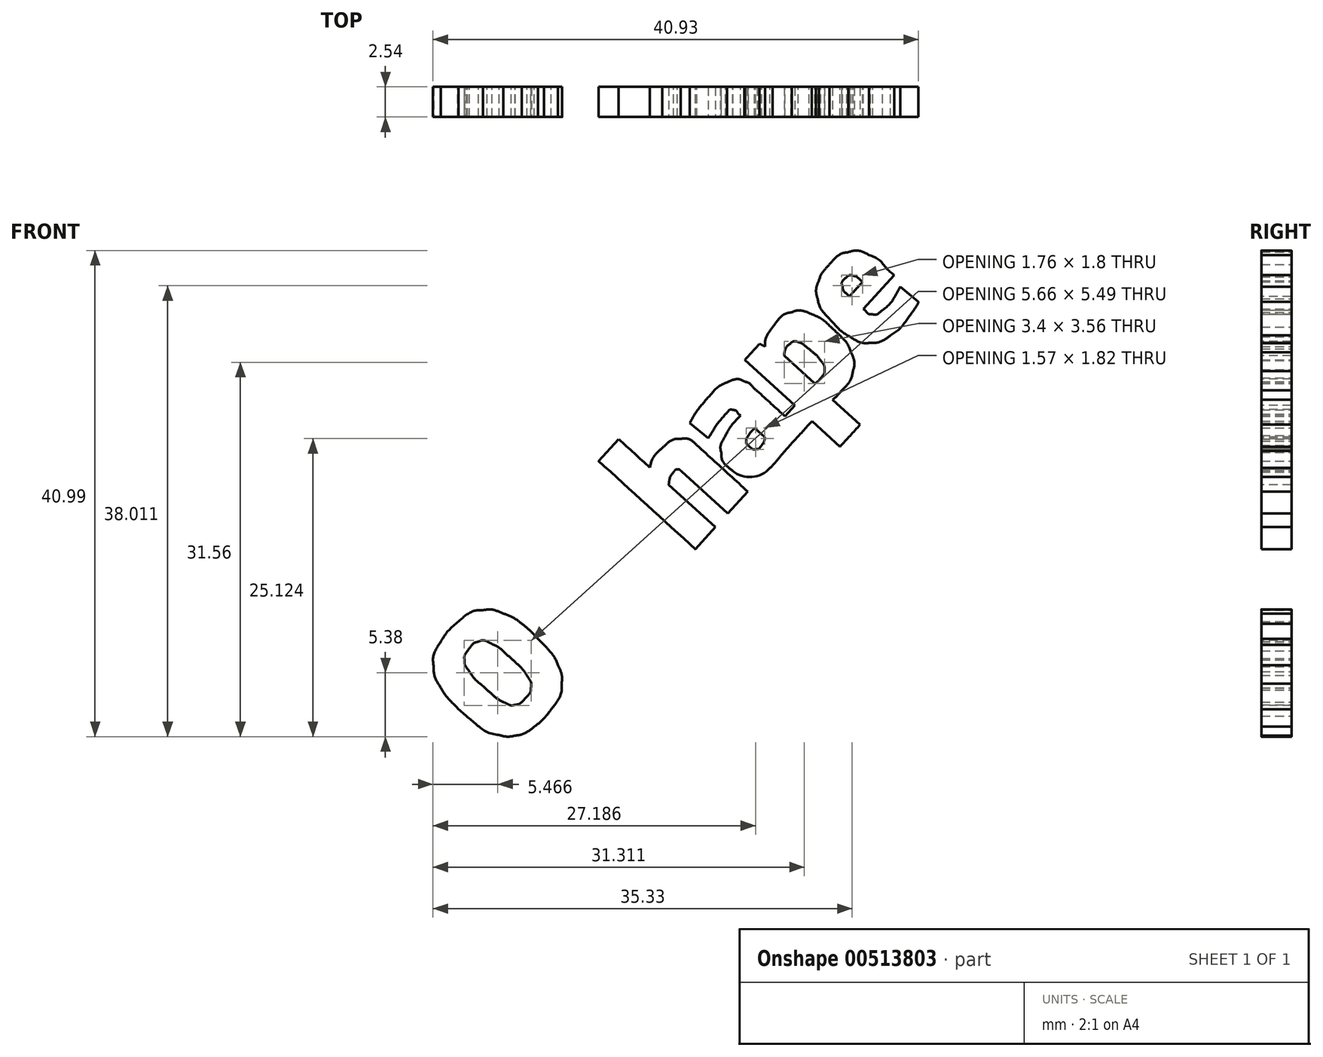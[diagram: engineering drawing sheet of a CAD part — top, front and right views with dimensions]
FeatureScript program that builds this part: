
annotation { "Feature Type Name" : "Feature", "Feature Type Description" : "" }
export const myFeature = defineFeature(function(context is Context, id is Id, definition is map)
    precondition{}
    {
        {
            var Q0;
            Q0=qCreatedBy(makeId("Front.planeOp"),FACE);
            var sketch = newSketch(context, id + "F0", { "sketchPlane" : qUnion([Q0])});
            skLineSegment(sketch, "E0", {"start": v(-53.27, 10.23) * mm, "end": v(-36.43, 28.71) * mm});
            skFitSpline(sketch, "E1", {"points": [v(-36.43, 28.71) * mm, v(-27.64, 20.71) * mm, v(-18.87, 12.7) * mm, v(-10.08, 4.7) * mm]});
            skFitSpline(sketch, "E2", {"points": [v(-10.08, 4.7) * mm, v(-8.44, 11.15) * mm, v(-4.52, 16.83) * mm, v(0.34, 21.3) * mm]});
            skFitSpline(sketch, "E3", {"points": [v(0.34, 21.3) * mm, v(4.57, 25.2) * mm, v(9.8, 28.49) * mm, v(15.67, 28.9) * mm]});
            skFitSpline(sketch, "E4", {"points": [v(15.67, 28.9) * mm, v(20.8, 29.27) * mm, v(25.8, 26.98) * mm, v(29.52, 23.56) * mm]});
            skFitSpline(sketch, "E5", {"points": [v(29.52, 23.56) * mm, v(43.78, 10.53) * mm, v(58.1, -2.45) * mm, v(72.33, -15.5) * mm]});
            skFitSpline(sketch, "E6", {"points": [v(72.33, -15.5) * mm, v(66.71, -21.65) * mm, v(61.11, -27.81) * mm, v(55.5, -33.96) * mm]});
            skFitSpline(sketch, "E7", {"points": [v(55.5, -33.96) * mm, v(42.52, -22.13) * mm, v(29.54, -10.3) * mm, v(16.56, 1.53) * mm]});
            skFitSpline(sketch, "E8", {"points": [v(16.56, 1.53) * mm, v(15.6, 2.38) * mm, v(14.46, 3.32) * mm, v(13.1, 3.21) * mm]});
            skFitSpline(sketch, "E9", {"points": [v(13.1, 3.21) * mm, v(11.64, 3.07) * mm, v(10.56, 1.91) * mm, v(9.69, 0.84) * mm]});
            skFitSpline(sketch, "E10", {"points": [v(9.69, 0.84) * mm, v(7.37, -2.2) * mm, v(6.21, -5.96) * mm, v(5.73, -9.7) * mm]});
            skFitSpline(sketch, "E11", {"points": [v(5.73, -9.7) * mm, v(18.8, -21.64) * mm, v(31.9, -33.56) * mm, v(44.98, -45.5) * mm]});
            skFitSpline(sketch, "E12", {"points": [v(44.98, -45.5) * mm, v(39.37, -51.66) * mm, v(33.75, -57.82) * mm, v(28.14, -63.97) * mm]});
            skFitSpline(sketch, "E13", {"points": [v(28.14, -63.97) * mm, v(1, -39.24) * mm, v(-26.13, -14.5) * mm, v(-53.27, 10.23) * mm]});
            skFitSpline(sketch, "E14", {"points": [v(-186.33, -141.9) * mm, v(-182.32, -135.58) * mm, v(-177.27, -129.94) * mm, v(-171.6, -125.06) * mm]});
            skFitSpline(sketch, "E15", {"points": [v(-171.6, -125.06) * mm, v(-165.71, -120.05) * mm, v(-158.56, -116.1) * mm, v(-150.74, -115.42) * mm]});
            skFitSpline(sketch, "E16", {"points": [v(-150.74, -115.42) * mm, v(-144.9, -114.85) * mm, v(-139.02, -116.11) * mm, v(-133.65, -118.36) * mm]});
            skFitSpline(sketch, "E17", {"points": [v(-133.65, -118.36) * mm, v(-126.81, -120.95) * mm, v(-120.6, -124.93) * mm, v(-114.78, -129.3) * mm]});
            skFitSpline(sketch, "E18", {"points": [v(-120.21, -125.1) * mm, v(-114.66, -129.62) * mm, v(-109.39, -134.5) * mm, v(-104.55, -139.78) * mm]});
            skFitSpline(sketch, "E19", {"points": [v(-99.47, -144.6) * mm, v(-94.8, -149.75) * mm, v(-90.53, -155.38) * mm, v(-87.66, -161.75) * mm]});
            skFitSpline(sketch, "E20", {"points": [v(-87.66, -161.75) * mm, v(-85.46, -166.63) * mm, v(-84.22, -172) * mm, v(-84.54, -177.37) * mm]});
            skFitSpline(sketch, "E21", {"points": [v(-84.54, -177.37) * mm, v(-84.95, -185.4) * mm, v(-88.7, -192.85) * mm, v(-93.46, -199.17) * mm]});
            skFitSpline(sketch, "E22", {"points": [v(-93.46, -199.17) * mm, v(-97.55, -204.52) * mm, v(-102.2, -209.48) * mm, v(-107.55, -213.6) * mm]});
            skFitSpline(sketch, "E23", {"points": [v(-107.55, -213.6) * mm, v(-112.33, -217.28) * mm, v(-117.85, -220.17) * mm, v(-123.83, -221.24) * mm]});
            skFitSpline(sketch, "E24", {"points": [v(-123.83, -221.24) * mm, v(-128.3, -222.06) * mm, v(-132.96, -221.8) * mm, v(-137.37, -220.7) * mm]});
            skFitSpline(sketch, "E25", {"points": [v(-137.37, -220.7) * mm, v(-147.8, -218.04) * mm, v(-156.69, -211.53) * mm, v(-164.86, -204.77) * mm]});
            skLineSegment(sketch, "E26", {"start": v(-164.86, -204.77) * mm, "end": v(-172.01, -198.25) * mm});
            skFitSpline(sketch, "E27", {"points": [v(-172.01, -198.25) * mm, v(-177.2, -193.04) * mm, v(-182.25, -187.58) * mm, v(-186.12, -181.29) * mm]});
            skFitSpline(sketch, "E28", {"points": [v(-186.12, -181.29) * mm, v(-189.52, -175.81) * mm, v(-192.02, -169.62) * mm, v(-192.4, -163.13) * mm]});
            skFitSpline(sketch, "E29", {"points": [v(-192.4, -163.13) * mm, v(-192.9, -155.61) * mm, v(-190.31, -148.2) * mm, v(-186.33, -141.9) * mm]});
            skFitSpline(sketch, "E30", {"points": [v(-164.02, -149.89) * mm, v(-165.55, -152.09) * mm, v(-166.58, -154.74) * mm, v(-166.4, -157.46) * mm]});
            skFitSpline(sketch, "E31", {"points": [v(-166.4, -157.46) * mm, v(-166.2, -161.13) * mm, v(-164.3, -164.44) * mm, v(-162.22, -167.37) * mm]});
            skFitSpline(sketch, "E32", {"points": [v(-162.22, -167.37) * mm, v(-157.95, -173.21) * mm, v(-152.58, -178.12) * mm, v(-147.22, -182.95) * mm]});
            skFitSpline(sketch, "E33", {"points": [v(-147.22, -182.95) * mm, v(-142.97, -186.63) * mm, v(-138.6, -190.25) * mm, v(-133.62, -192.9) * mm]});
            skFitSpline(sketch, "E34", {"points": [v(-133.62, -192.9) * mm, v(-130.57, -194.5) * mm, v(-127.07, -195.74) * mm, v(-123.58, -195.13) * mm]});
            skFitSpline(sketch, "E35", {"points": [v(-123.58, -195.13) * mm, v(-120.22, -194.56) * mm, v(-117.48, -192.3) * mm, v(-115.22, -189.88) * mm]});
            skFitSpline(sketch, "E36", {"points": [v(-115.22, -189.88) * mm, v(-112.92, -187.36) * mm, v(-110.77, -184.36) * mm, v(-110.47, -180.85) * mm]});
            skFitSpline(sketch, "E37", {"points": [v(-110.47, -180.85) * mm, v(-110.14, -177.1) * mm, v(-111.87, -173.56) * mm, v(-113.88, -170.52) * mm]});
            skFitSpline(sketch, "E38", {"points": [v(-113.88, -170.52) * mm, v(-117.56, -165.1) * mm, v(-122.34, -160.58) * mm, v(-127.1, -156.13) * mm]});
            skFitSpline(sketch, "E39", {"points": [v(-127.1, -156.13) * mm, v(-132.17, -151.63) * mm, v(-137.33, -147.07) * mm, v(-143.37, -143.9) * mm]});
            skFitSpline(sketch, "E40", {"points": [v(-143.37, -143.9) * mm, v(-146.8, -142.1) * mm, v(-150.9, -140.83) * mm, v(-154.74, -142.07) * mm]});
            skFitSpline(sketch, "E41", {"points": [v(-154.74, -142.07) * mm, v(-158.68, -143.4) * mm, v(-161.63, -146.62) * mm, v(-164.02, -149.89) * mm]});
            skFitSpline(sketch, "E42", {"points": [v(-104.03, -102.52) * mm, v(-103.02, -94.53) * mm, v(-99.15, -87) * mm, v(-93.41, -81.38) * mm]});
            skFitSpline(sketch, "E43", {"points": [v(-93.41, -81.38) * mm, v(-89.05, -77.02) * mm, v(-83.58, -73.2) * mm, v(-77.29, -72.58) * mm]});
            skFitSpline(sketch, "E44", {"points": [v(-77.29, -72.58) * mm, v(-72.12, -72.02) * mm, v(-67.02, -74.23) * mm, v(-63.2, -77.62) * mm]});
            skFitSpline(sketch, "E45", {"points": [v(-63.2, -77.62) * mm, v(-53.68, -86.29) * mm, v(-44.17, -94.97) * mm, v(-34.64, -103.65) * mm]});
            skFitSpline(sketch, "E46", {"points": [v(-10.06, -76.67) * mm, v(-9.19, -75.62) * mm, v(-8.13, -74.65) * mm, v(-7.6, -73.37) * mm]});
            skFitSpline(sketch, "E47", {"points": [v(-7.6, -73.37) * mm, v(-7.12, -72.25) * mm, v(-8.15, -71.15) * mm, v(-9.12, -70.75) * mm]});
            skFitSpline(sketch, "E48", {"points": [v(-9.12, -70.75) * mm, v(-10.63, -70.2) * mm, v(-12.23, -70.8) * mm, v(-13.63, -71.35) * mm]});
            skFitSpline(sketch, "E49", {"points": [v(-13.63, -71.35) * mm, v(-17.16, -72.88) * mm, v(-20.68, -74.43) * mm, v(-24.2, -75.97) * mm]});
            skFitSpline(sketch, "E50", {"points": [v(-24.2, -75.97) * mm, v(-27.72, -77.47) * mm, v(-31.17, -79.28) * mm, v(-35, -79.83) * mm]});
            skFitSpline(sketch, "E51", {"points": [v(-35, -79.83) * mm, v(-40.54, -80.8) * mm, v(-46.38, -79.42) * mm, v(-51.02, -76.27) * mm]});
            skFitSpline(sketch, "E52", {"points": [v(-51.02, -76.27) * mm, v(-55.75, -73.06) * mm, v(-59.9, -68.53) * mm, v(-61.46, -62.93) * mm]});
            skFitSpline(sketch, "E53", {"points": [v(-61.46, -62.93) * mm, v(-62.78, -58.27) * mm, v(-62.02, -53.26) * mm, v(-60.19, -48.85) * mm]});
            skFitSpline(sketch, "E54", {"points": [v(-60.19, -48.85) * mm, v(-57.48, -42.27) * mm, v(-52.9, -36.68) * mm, v(-48.03, -31.57) * mm]});
            skFitSpline(sketch, "E55", {"points": [v(-48.03, -31.57) * mm, v(-43.95, -27.33) * mm, v(-39.76, -23.17) * mm, v(-35.17, -19.47) * mm]});
            skFitSpline(sketch, "E56", {"points": [v(-35.17, -19.47) * mm, v(-30.45, -24.14) * mm, v(-25.78, -28.86) * mm, v(-21.09, -33.56) * mm]});
            skFitSpline(sketch, "E57", {"points": [v(-21.09, -33.56) * mm, v(-24.53, -36.31) * mm, v(-27.72, -39.36) * mm, v(-30.85, -42.46) * mm]});
            skFitSpline(sketch, "E58", {"points": [v(-30.85, -42.46) * mm, v(-32.92, -44.54) * mm, v(-35, -46.61) * mm, v(-36.84, -48.9) * mm]});
            skFitSpline(sketch, "E59", {"points": [v(-36.84, -48.9) * mm, v(-37.61, -49.94) * mm, v(-38.46, -51.03) * mm, v(-38.61, -52.35) * mm]});
            skFitSpline(sketch, "E60", {"points": [v(-38.61, -52.35) * mm, v(-38.74, -53.52) * mm, v(-37.78, -54.45) * mm, v(-36.82, -54.95) * mm]});
            skFitSpline(sketch, "E61", {"points": [v(-36.82, -54.95) * mm, v(-35.8, -55.43) * mm, v(-34.65, -55.1) * mm, v(-33.66, -54.72) * mm]});
            skFitSpline(sketch, "E62", {"points": [v(-33.66, -54.72) * mm, v(-27.51, -52.21) * mm, v(-21.4, -49.63) * mm, v(-15.25, -47.13) * mm]});
            skFitSpline(sketch, "E63", {"points": [v(-15.25, -47.13) * mm, v(-10.1, -45.1) * mm, v(-4.15, -44.97) * mm, v(0.92, -47.28) * mm]});
            skFitSpline(sketch, "E64", {"points": [v(0.92, -47.28) * mm, v(5.88, -49.54) * mm, v(10.08, -53.4) * mm, v(12.97, -58) * mm]});
            skFitSpline(sketch, "E65", {"points": [v(12.97, -58) * mm, v(16.03, -62.29) * mm, v(17.14, -67.82) * mm, v(16.14, -72.98) * mm]});
            skFitSpline(sketch, "E66", {"points": [v(-36.98, -135.4) * mm, v(-50.22, -123.37) * mm, v(-63.42, -111.28) * mm, v(-76.67, -99.25) * mm]});
            skFitSpline(sketch, "E67", {"points": [v(-76.67, -99.25) * mm, v(-77.91, -98.04) * mm, v(-79.99, -97.82) * mm, v(-81.29, -99.06) * mm]});
            skFitSpline(sketch, "E68", {"points": [v(-81.29, -99.06) * mm, v(-84.7, -102.09) * mm, v(-86.12, -106.73) * mm, v(-86.73, -111.12) * mm]});
            skFitSpline(sketch, "E69", {"points": [v(-86.73, -111.12) * mm, v(-73.65, -123.06) * mm, v(-60.55, -134.98) * mm, v(-47.47, -146.91) * mm]});
            skFitSpline(sketch, "E70", {"points": [v(-47.47, -146.91) * mm, v(-53.1, -153.09) * mm, v(-58.72, -159.25) * mm, v(-64.34, -165.42) * mm]});
            skFitSpline(sketch, "E71", {"points": [v(-120.95, -113.82) * mm, v(-116.84, -109.3) * mm, v(-112.71, -104.79) * mm, v(-108.6, -100.27) * mm]});
            skFitSpline(sketch, "E72", {"points": [v(-108.6, -100.27) * mm, v(-107.07, -101.02) * mm, v(-105.55, -101.77) * mm, v(-104.03, -102.52) * mm]});
            skFitSpline(sketch, "E73", {"points": [v(23.54, 42.35) * mm, v(27.53, 49.45) * mm, v(32.32, 56.09) * mm, v(37.57, 62.3) * mm]});
            skFitSpline(sketch, "E74", {"points": [v(37.57, 62.3) * mm, v(42.46, 67.97) * mm, v(48.03, 73.34) * mm, v(54.92, 76.47) * mm]});
            skFitSpline(sketch, "E75", {"points": [v(54.92, 76.47) * mm, v(59.47, 78.56) * mm, v(64.89, 79.24) * mm, v(69.62, 77.33) * mm]});
            skFitSpline(sketch, "E76", {"points": [v(69.62, 77.33) * mm, v(73.88, 75.73) * mm, v(76.98, 72.26) * mm, v(80.3, 69.33) * mm]});
            skFitSpline(sketch, "E77", {"points": [v(80.3, 69.33) * mm, v(88.09, 62.24) * mm, v(95.86, 55.14) * mm, v(103.65, 48.05) * mm]});
            skFitSpline(sketch, "E78", {"points": [v(103.65, 48.05) * mm, v(106.44, 51.12) * mm, v(109.23, 54.18) * mm, v(112.02, 57.24) * mm]});
            skFitSpline(sketch, "E79", {"points": [v(112.02, 57.24) * mm, v(98, 70.03) * mm, v(83.97, 82.8) * mm, v(69.95, 95.6) * mm]});
            skFitSpline(sketch, "E80", {"points": [v(69.95, 95.6) * mm, v(74.07, 100.1) * mm, v(78.18, 104.63) * mm, v(82.3, 109.13) * mm]});
            skFitSpline(sketch, "E81", {"points": [v(82.3, 109.13) * mm, v(83.82, 108.38) * mm, v(85.35, 107.63) * mm, v(86.88, 106.89) * mm]});
            skFitSpline(sketch, "E82", {"points": [v(86.88, 106.89) * mm, v(87.24, 112.8) * mm, v(89.9, 118.34) * mm, v(93.32, 123.1) * mm]});
            skFitSpline(sketch, "E83", {"points": [v(93.32, 123.1) * mm, v(97.36, 128.62) * mm, v(102.62, 133.75) * mm, v(109.37, 135.66) * mm]});
            skFitSpline(sketch, "E84", {"points": [v(109.37, 135.66) * mm, v(114.94, 137.28) * mm, v(120.96, 136.3) * mm, v(126.2, 134) * mm]});
            skFitSpline(sketch, "E85", {"points": [v(126.2, 134) * mm, v(133.7, 130.74) * mm, v(140.1, 125.47) * mm, v(146.02, 119.92) * mm]});
            skFitSpline(sketch, "E86", {"points": [v(146.02, 119.92) * mm, v(151.44, 114.7) * mm, v(156.47, 108.83) * mm, v(159.4, 101.83) * mm]});
            skFitSpline(sketch, "E87", {"points": [v(159.4, 101.83) * mm, v(161.5, 96.85) * mm, v(162.2, 91.23) * mm, v(160.95, 85.94) * mm]});
            skFitSpline(sketch, "E88", {"points": [v(160.95, 85.94) * mm, v(159.56, 79.83) * mm, v(156.01, 74.43) * mm, v(151.82, 69.86) * mm]});
            skFitSpline(sketch, "E89", {"points": [v(151.82, 69.86) * mm, v(149.32, 67.12) * mm, v(146.73, 64.47) * mm, v(143.9, 62.07) * mm]});
            skFitSpline(sketch, "E90", {"points": [v(143.9, 62.07) * mm, v(151.63, 55.03) * mm, v(159.36, 47.98) * mm, v(167.09, 40.94) * mm]});
            skFitSpline(sketch, "E91", {"points": [v(167.09, 40.94) * mm, v(161.47, 34.76) * mm, v(155.84, 28.6) * mm, v(150.22, 22.43) * mm]});
            skFitSpline(sketch, "E92", {"points": [v(150.22, 22.43) * mm, v(142.33, 29.61) * mm, v(134.45, 36.8) * mm, v(126.56, 43.99) * mm]});
            skFitSpline(sketch, "E93", {"points": [v(126.56, 43.99) * mm, v(118.91, 35.6) * mm, v(111.25, 27.22) * mm, v(103.62, 18.81) * mm]});
            skFitSpline(sketch, "E94", {"points": [v(103.62, 18.81) * mm, v(99.56, 13.9) * mm, v(95.51, 8.97) * mm, v(91.11, 4.37) * mm]});
            skFitSpline(sketch, "E95", {"points": [v(59.52, 2.02) * mm, v(54.7, 5.92) * mm, v(50.7, 11.35) * mm, v(49.95, 17.64) * mm]});
            skFitSpline(sketch, "E96", {"points": [v(49.95, 17.64) * mm, v(49.3, 22.63) * mm, v(51.31, 27.47) * mm, v(53.6, 31.79) * mm]});
            skFitSpline(sketch, "E97", {"points": [v(53.6, 31.79) * mm, v(57, 37.98) * mm, v(61.42, 43.54) * mm, v(66.15, 48.75) * mm]});
            skFitSpline(sketch, "E98", {"points": [v(66.15, 48.75) * mm, v(64.17, 50.33) * mm, v(62.57, 52.7) * mm, v(59.97, 53.27) * mm]});
            skFitSpline(sketch, "E99", {"points": [v(59.97, 53.27) * mm, v(57.4, 53.67) * mm, v(55.35, 51.63) * mm, v(53.74, 49.92) * mm]});
            skFitSpline(sketch, "E100", {"points": [v(53.74, 49.92) * mm, v(48.26, 43.55) * mm, v(43.43, 36.64) * mm, v(39.1, 29.44) * mm]});
            skFitSpline(sketch, "E101", {"points": [v(39.1, 29.44) * mm, v(33.91, 33.75) * mm, v(28.72, 38.05) * mm, v(23.54, 42.35) * mm]});
            skFitSpline(sketch, "E102", {"points": [v(103.13, 99.24) * mm, v(111.74, 91.4) * mm, v(120.34, 83.54) * mm, v(128.96, 75.7) * mm]});
            skFitSpline(sketch, "E103", {"points": [v(128.96, 75.7) * mm, v(130.89, 76.93) * mm, v(132.55, 78.55) * mm, v(134, 80.32) * mm]});
            skFitSpline(sketch, "E104", {"points": [v(134, 80.32) * mm, v(135.6, 82.3) * mm, v(136.93, 84.71) * mm, v(136.95, 87.33) * mm]});
            skFitSpline(sketch, "E105", {"points": [v(136.95, 87.33) * mm, v(136.97, 90.21) * mm, v(135.48, 92.84) * mm, v(133.8, 95.07) * mm]});
            skFitSpline(sketch, "E106", {"points": [v(133.8, 95.07) * mm, v(130.98, 98.7) * mm, v(127.5, 101.75) * mm, v(124.02, 104.72) * mm]});
            skFitSpline(sketch, "E107", {"points": [v(124.02, 104.72) * mm, v(121.2, 107) * mm, v(118.28, 109.32) * mm, v(114.81, 110.5) * mm]});
            skFitSpline(sketch, "E108", {"points": [v(114.81, 110.5) * mm, v(112.79, 111.22) * mm, v(110.4, 111.04) * mm, v(108.69, 109.68) * mm]});
            skFitSpline(sketch, "E109", {"points": [v(108.69, 109.68) * mm, v(105.5, 107.16) * mm, v(103.56, 103.24) * mm, v(103.13, 99.24) * mm]});
            skFitSpline(sketch, "E110", {"points": [v(72.95, 31.92) * mm, v(72, 30.49) * mm, v(71.1, 28.89) * mm, v(71.08, 27.12) * mm]});
            skFitSpline(sketch, "E111", {"points": [v(71.08, 27.12) * mm, v(71.12, 25.34) * mm, v(72.27, 23.79) * mm, v(73.54, 22.63) * mm]});
            skFitSpline(sketch, "E112", {"points": [v(73.54, 22.63) * mm, v(75.03, 21.3) * mm, v(76.92, 20.12) * mm, v(79, 20.26) * mm]});
            skFitSpline(sketch, "E113", {"points": [v(79, 20.26) * mm, v(81.13, 20.42) * mm, v(82.9, 21.93) * mm, v(84.13, 23.58) * mm]});
            skFitSpline(sketch, "E114", {"points": [v(84.13, 23.58) * mm, v(85.55, 25.6) * mm, v(86.56, 27.96) * mm, v(86.7, 30.44) * mm]});
            skFitSpline(sketch, "E115", {"points": [v(86.7, 30.44) * mm, v(83.85, 33.03) * mm, v(81, 35.63) * mm, v(78.16, 38.22) * mm]});
            skFitSpline(sketch, "E116", {"points": [v(78.16, 38.22) * mm, v(76.34, 36.2) * mm, v(74.49, 34.18) * mm, v(72.95, 31.92) * mm]});
            skFitSpline(sketch, "E117", {"points": [v(132.26, 162.28) * mm, v(134.22, 167.42) * mm, v(137.48, 171.96) * mm, v(141.15, 176) * mm]});
            skFitSpline(sketch, "E118", {"points": [v(141.15, 176) * mm, v(145.43, 180.8) * mm, v(150.85, 184.9) * mm, v(157.2, 186.37) * mm]});
            skFitSpline(sketch, "E119", {"points": [v(157.2, 186.37) * mm, v(163.06, 187.77) * mm, v(169.27, 186.6) * mm, v(174.6, 183.97) * mm]});
            skFitSpline(sketch, "E120", {"points": [v(174.6, 183.97) * mm, v(182.89, 180.01) * mm, v(189.07, 173.04) * mm, v(195.87, 167.1) * mm]});
            skFitSpline(sketch, "E121", {"points": [v(195.87, 167.1) * mm, v(187.17, 157.54) * mm, v(178.46, 148) * mm, v(169.76, 138.44) * mm]});
            skFitSpline(sketch, "E122", {"points": [v(169.76, 138.44) * mm, v(172.04, 136.48) * mm, v(174.48, 134.22) * mm, v(177.63, 133.94) * mm]});
            skFitSpline(sketch, "E123", {"points": [v(177.63, 133.94) * mm, v(180.8, 133.72) * mm, v(183.59, 135.62) * mm, v(185.91, 137.55) * mm]});
            skFitSpline(sketch, "E124", {"points": [v(185.91, 137.55) * mm, v(192.24, 142.96) * mm, v(196.9, 150.02) * mm, v(200.82, 157.3) * mm]});
            skFitSpline(sketch, "E125", {"points": [v(200.82, 157.3) * mm, v(205.97, 153.02) * mm, v(211.13, 148.76) * mm, v(216.27, 144.48) * mm]});
            skFitSpline(sketch, "E126", {"points": [v(216.27, 144.48) * mm, v(214.74, 141.13) * mm, v(212.67, 138.06) * mm, v(210.55, 135.06) * mm]});
            skFitSpline(sketch, "E127", {"points": [v(210.55, 135.06) * mm, v(205.48, 128) * mm, v(199.78, 121.22) * mm, v(192.65, 116.17) * mm]});
            skFitSpline(sketch, "E128", {"points": [v(192.65, 116.17) * mm, v(187.77, 112.72) * mm, v(182.03, 110.2) * mm, v(176, 109.99) * mm]});
            skFitSpline(sketch, "E129", {"points": [v(176, 109.99) * mm, v(169.84, 109.7) * mm, v(163.83, 111.86) * mm, v(158.63, 115) * mm]});
            skFitSpline(sketch, "E130", {"points": [v(158.63, 115) * mm, v(152.39, 118.8) * mm, v(146.98, 123.81) * mm, v(142.02, 129.13) * mm]});
            skFitSpline(sketch, "E131", {"points": [v(142.02, 129.13) * mm, v(137.33, 134.29) * mm, v(133.08, 140.17) * mm, v(131.31, 147.02) * mm]});
            skFitSpline(sketch, "E132", {"points": [v(131.31, 147.02) * mm, v(130, 152.04) * mm, v(130.38, 157.45) * mm, v(132.26, 162.28) * mm]});
            skFitSpline(sketch, "E133", {"points": [v(152.2, 157.45) * mm, v(152.95, 154.01) * mm, v(155.61, 151.46) * mm, v(157.96, 149) * mm]});
            skFitSpline(sketch, "E134", {"points": [v(157.96, 149) * mm, v(161.67, 153.07) * mm, v(165.37, 157.14) * mm, v(169.08, 161.2) * mm]});
            skFitSpline(sketch, "E135", {"points": [v(169.08, 161.2) * mm, v(166.82, 163.3) * mm, v(164.42, 165.5) * mm, v(161.4, 166.4) * mm]});
            skFitSpline(sketch, "E136", {"points": [v(161.4, 166.4) * mm, v(159.47, 167) * mm, v(157.29, 166.61) * mm, v(155.73, 165.33) * mm]});
            skFitSpline(sketch, "E137", {"points": [v(155.73, 165.33) * mm, v(153.47, 163.44) * mm, v(151.56, 160.51) * mm, v(152.2, 157.45) * mm]});
            skLineSegment(sketch, "E138", {"start": v(-104.55, -139.78) * mm, "end": v(-99.47, -144.6) * mm});
            skLineSegment(sketch, "E139", {"start": v(-64.34, -165.42) * mm, "end": v(-119.6, -112.33) * mm});
            skFitSpline(sketch, "E140.trimOffspring", {"points": [v(158.63, 115) * mm, v(152.39, 118.8) * mm, v(146.98, 123.81) * mm, v(142.02, 129.13) * mm]});
            skLineSegment(sketch, "E141", {"start": v(65.71, -9.44) * mm, "end": v(72.33, -15.5) * mm});
            skArc(sketch, "E142", {"start": v(10.7, -83.15) * mm, "mid": v(13.97, -78.34) * mm, "end": v(16.15, -72.95) * mm});
            skLineSegment(sketch, "E143", {"start": v(21.51, -57.93) * mm, "end": v(28.14, -63.97) * mm});
            skArc(sketch, "E144", {"start": v(59.52, 2.02) * mm, "mid": v(75.79, -3.17) * mm, "end": v(91.11, 4.37) * mm});
            skLineSegment(sketch, "E145", {"start": v(-34.64, -103.65) * mm, "end": v(-10.06, -76.67) * mm});
            skLineSegment(sketch, "E146", {"start": v(-36.98, -135.4) * mm, "end": v(10.7, -83.15) * mm});
            skLineSegment(sketch, "E147", {"start": v(143, 122.67) * mm, "end": v(149.04, 116.89) * mm});
            skLineSegment(sketch, "E148", {"start": v(145.56, 125.48) * mm, "end": v(151.76, 119.88) * mm});
            skSolve(sketch);
        }
        {
            var Q0;
            Q0=makeQuery(id+"F0.imprint","IMPRINT",FACE,{"disambiguationData":[TD([[makeQuery(id+"F0.imprint","IMPRINT",EDGE,{"derivedFrom":sQuery(id+"F0.wireOp",EDGE,"E14")}),-1.0]])]});
            var Q1;
            Q1=makeQuery(id+"F0.imprint","IMPRINT",FACE,{"disambiguationData":[TD([[makeQuery(id+"F0.imprint","IMPRINT",EDGE,{"derivedFrom":sQuery(id+"F0.wireOp",EDGE,"E42")}),-1.0]])]});
            var Q2;
            Q2=makeQuery(id+"F0.imprint","IMPRINT",FACE,{"disambiguationData":[TD([[makeQuery(id+"F0.imprint","IMPRINT",EDGE,{"derivedFrom":sQuery(id+"F0.wireOp",EDGE,"E0")}),-1.0]])]});
            var Q3;
            Q3=makeQuery(id+"F0.imprint","IMPRINT",FACE,{"disambiguationData":[TD([[makeQuery(id+"F0.imprint","IMPRINT",EDGE,{"derivedFrom":sQuery(id+"F0.wireOp",EDGE,"E73")}),-1.0]])]});
            var Q4;
            Q4=makeQuery(id+"F0.imprint","IMPRINT",FACE,{"disambiguationData":[TD([[makeQuery(id+"F0.imprint","IMPRINT",EDGE,{"derivedFrom":sQuery(id+"F0.wireOp",EDGE,"E117")}),-1.0]])]});
            extrude(context, id + "F1", {"entities" : qUnion([Q0, Q1, Q2, Q3, Q4]), "depth" : 25.4 * mm, "offsetDistance" : 25.4 * mm});
        }
        {
            var Q0;
            Q0=makeQuery(id+"F1.opExtrude","SWEPT_BODY",BODY,{"disambiguationData":[OSD([sQuery(id+"F0.wireOp",EDGE,"E0"),sQuery(id+"F0.wireOp",EDGE,"E1"),sQuery(id+"F0.wireOp",EDGE,"E2"),sQuery(id+"F0.wireOp",EDGE,"E3"),sQuery(id+"F0.wireOp",EDGE,"E4"),sQuery(id+"F0.wireOp",EDGE,"E5"),sQuery(id+"F0.wireOp",EDGE,"E6"),sQuery(id+"F0.wireOp",EDGE,"E7"),sQuery(id+"F0.wireOp",EDGE,"E8"),sQuery(id+"F0.wireOp",EDGE,"E9"),sQuery(id+"F0.wireOp",EDGE,"E10"),sQuery(id+"F0.wireOp",EDGE,"E11"),sQuery(id+"F0.wireOp",EDGE,"E12"),sQuery(id+"F0.wireOp",EDGE,"E13"),sQuery(id+"F0.wireOp",EDGE,"E141"),sQuery(id+"F0.wireOp",EDGE,"E143")])]});
            var Q1;
            Q1=makeQuery(id+"F1.opExtrude","SWEPT_BODY",BODY,{"disambiguationData":[OSD([sQuery(id+"F0.wireOp",EDGE,"E117"),sQuery(id+"F0.wireOp",EDGE,"E118"),sQuery(id+"F0.wireOp",EDGE,"E119"),sQuery(id+"F0.wireOp",EDGE,"E120"),sQuery(id+"F0.wireOp",EDGE,"E121"),sQuery(id+"F0.wireOp",EDGE,"E122"),sQuery(id+"F0.wireOp",EDGE,"E123"),sQuery(id+"F0.wireOp",EDGE,"E124"),sQuery(id+"F0.wireOp",EDGE,"E125"),sQuery(id+"F0.wireOp",EDGE,"E126"),sQuery(id+"F0.wireOp",EDGE,"E127"),sQuery(id+"F0.wireOp",EDGE,"E128"),sQuery(id+"F0.wireOp",EDGE,"E129"),sQuery(id+"F0.wireOp",EDGE,"E130"),sQuery(id+"F0.wireOp",EDGE,"E131"),sQuery(id+"F0.wireOp",EDGE,"E132"),sQuery(id+"F0.wireOp",EDGE,"E133"),sQuery(id+"F0.wireOp",EDGE,"E134"),sQuery(id+"F0.wireOp",EDGE,"E135"),sQuery(id+"F0.wireOp",EDGE,"E136"),sQuery(id+"F0.wireOp",EDGE,"E137"),sQuery(id+"F0.wireOp",EDGE,"E140.trimOffspring"),sQuery(id+"F0.wireOp",EDGE,"E148")])]});
            var Q2;
            Q2=makeQuery(id+"F1.opExtrude","SWEPT_BODY",BODY,{"disambiguationData":[OSD([sQuery(id+"F0.wireOp",EDGE,"E42"),sQuery(id+"F0.wireOp",EDGE,"E43"),sQuery(id+"F0.wireOp",EDGE,"E44"),sQuery(id+"F0.wireOp",EDGE,"E45"),sQuery(id+"F0.wireOp",EDGE,"E46"),sQuery(id+"F0.wireOp",EDGE,"E47"),sQuery(id+"F0.wireOp",EDGE,"E48"),sQuery(id+"F0.wireOp",EDGE,"E49"),sQuery(id+"F0.wireOp",EDGE,"E50"),sQuery(id+"F0.wireOp",EDGE,"E51"),sQuery(id+"F0.wireOp",EDGE,"E52"),sQuery(id+"F0.wireOp",EDGE,"E53"),sQuery(id+"F0.wireOp",EDGE,"E54"),sQuery(id+"F0.wireOp",EDGE,"E55"),sQuery(id+"F0.wireOp",EDGE,"E56"),sQuery(id+"F0.wireOp",EDGE,"E57"),sQuery(id+"F0.wireOp",EDGE,"E58"),sQuery(id+"F0.wireOp",EDGE,"E59"),sQuery(id+"F0.wireOp",EDGE,"E60"),sQuery(id+"F0.wireOp",EDGE,"E61"),sQuery(id+"F0.wireOp",EDGE,"E62"),sQuery(id+"F0.wireOp",EDGE,"E63"),sQuery(id+"F0.wireOp",EDGE,"E64"),sQuery(id+"F0.wireOp",EDGE,"E65"),sQuery(id+"F0.wireOp",EDGE,"E66"),sQuery(id+"F0.wireOp",EDGE,"E67"),sQuery(id+"F0.wireOp",EDGE,"E68"),sQuery(id+"F0.wireOp",EDGE,"E69"),sQuery(id+"F0.wireOp",EDGE,"E70"),sQuery(id+"F0.wireOp",EDGE,"E71"),sQuery(id+"F0.wireOp",EDGE,"E72"),sQuery(id+"F0.wireOp",EDGE,"E139"),sQuery(id+"F0.wireOp",EDGE,"E142"),sQuery(id+"F0.wireOp",EDGE,"E145"),sQuery(id+"F0.wireOp",EDGE,"E146")])]});
            var Q3;
            Q3=makeQuery(id+"F1.opExtrude","SWEPT_BODY",BODY,{"disambiguationData":[OSD([sQuery(id+"F0.wireOp",EDGE,"E14"),sQuery(id+"F0.wireOp",EDGE,"E15"),sQuery(id+"F0.wireOp",EDGE,"E16"),sQuery(id+"F0.wireOp",EDGE,"E17"),sQuery(id+"F0.wireOp",EDGE,"E18"),sQuery(id+"F0.wireOp",EDGE,"E19"),sQuery(id+"F0.wireOp",EDGE,"E20"),sQuery(id+"F0.wireOp",EDGE,"E21"),sQuery(id+"F0.wireOp",EDGE,"E22"),sQuery(id+"F0.wireOp",EDGE,"E23"),sQuery(id+"F0.wireOp",EDGE,"E24"),sQuery(id+"F0.wireOp",EDGE,"E25"),sQuery(id+"F0.wireOp",EDGE,"E26"),sQuery(id+"F0.wireOp",EDGE,"E27"),sQuery(id+"F0.wireOp",EDGE,"E28"),sQuery(id+"F0.wireOp",EDGE,"E29"),sQuery(id+"F0.wireOp",EDGE,"E30"),sQuery(id+"F0.wireOp",EDGE,"E31"),sQuery(id+"F0.wireOp",EDGE,"E32"),sQuery(id+"F0.wireOp",EDGE,"E33"),sQuery(id+"F0.wireOp",EDGE,"E34"),sQuery(id+"F0.wireOp",EDGE,"E35"),sQuery(id+"F0.wireOp",EDGE,"E36"),sQuery(id+"F0.wireOp",EDGE,"E37"),sQuery(id+"F0.wireOp",EDGE,"E38"),sQuery(id+"F0.wireOp",EDGE,"E39"),sQuery(id+"F0.wireOp",EDGE,"E40"),sQuery(id+"F0.wireOp",EDGE,"E41"),sQuery(id+"F0.wireOp",EDGE,"E138")])]});
            var Q4;
            Q4=makeQuery(id+"F1.opExtrude","SWEPT_BODY",BODY,{"disambiguationData":[OSD([sQuery(id+"F0.wireOp",EDGE,"E73"),sQuery(id+"F0.wireOp",EDGE,"E74"),sQuery(id+"F0.wireOp",EDGE,"E75"),sQuery(id+"F0.wireOp",EDGE,"E76"),sQuery(id+"F0.wireOp",EDGE,"E77"),sQuery(id+"F0.wireOp",EDGE,"E78"),sQuery(id+"F0.wireOp",EDGE,"E79"),sQuery(id+"F0.wireOp",EDGE,"E80"),sQuery(id+"F0.wireOp",EDGE,"E81"),sQuery(id+"F0.wireOp",EDGE,"E82"),sQuery(id+"F0.wireOp",EDGE,"E83"),sQuery(id+"F0.wireOp",EDGE,"E84"),sQuery(id+"F0.wireOp",EDGE,"E85"),sQuery(id+"F0.wireOp",EDGE,"E86"),sQuery(id+"F0.wireOp",EDGE,"E87"),sQuery(id+"F0.wireOp",EDGE,"E88"),sQuery(id+"F0.wireOp",EDGE,"E89"),sQuery(id+"F0.wireOp",EDGE,"E90"),sQuery(id+"F0.wireOp",EDGE,"E91"),sQuery(id+"F0.wireOp",EDGE,"E92"),sQuery(id+"F0.wireOp",EDGE,"E93"),sQuery(id+"F0.wireOp",EDGE,"E94"),sQuery(id+"F0.wireOp",EDGE,"E95"),sQuery(id+"F0.wireOp",EDGE,"E96"),sQuery(id+"F0.wireOp",EDGE,"E97"),sQuery(id+"F0.wireOp",EDGE,"E98"),sQuery(id+"F0.wireOp",EDGE,"E99"),sQuery(id+"F0.wireOp",EDGE,"E100"),sQuery(id+"F0.wireOp",EDGE,"E101"),sQuery(id+"F0.wireOp",EDGE,"E102"),sQuery(id+"F0.wireOp",EDGE,"E103"),sQuery(id+"F0.wireOp",EDGE,"E104"),sQuery(id+"F0.wireOp",EDGE,"E105"),sQuery(id+"F0.wireOp",EDGE,"E106"),sQuery(id+"F0.wireOp",EDGE,"E107"),sQuery(id+"F0.wireOp",EDGE,"E108"),sQuery(id+"F0.wireOp",EDGE,"E109"),sQuery(id+"F0.wireOp",EDGE,"E110"),sQuery(id+"F0.wireOp",EDGE,"E111"),sQuery(id+"F0.wireOp",EDGE,"E112"),sQuery(id+"F0.wireOp",EDGE,"E113"),sQuery(id+"F0.wireOp",EDGE,"E114"),sQuery(id+"F0.wireOp",EDGE,"E115"),sQuery(id+"F0.wireOp",EDGE,"E116"),sQuery(id+"F0.wireOp",EDGE,"E144"),sQuery(id+"F0.wireOp",EDGE,"E147")])]});
            var Q5;
            Q5=qCreatedBy(makeId("Origin.pointOp"),VERTEX);
            transform(context, id + "F2", {"entities" : qUnion([Q0, Q1, Q2, Q3, Q4]), "transformType" : TransformType.SCALE_UNIFORMLY, "scale" : .1, "scalePoint" : qUnion([Q5]), "makeCopy" : false});
        }
    });
